# Revit family: Legrand XL³-S 630 24 Modules to the row
name_source: partatom
category: Equipement électrique
units: mm (PartAtom-declared; Revit-internal decimal feet)

## family parameters
Basée sur le plan de construction = Non
Configuration du panneau = Deux colonnes, circuits au sein
Cote de connecteur circulaire = Utiliser le diamètre
Couper avec des vides une fois chargée = Non
Numéro OmniClass = 23.80.30.11.17
Partagée = Non
Point de calcul de pièce = Non
Titre OmniClass = Distribution Boards and Control Panels
Toujours verticalement = Oui
Type d'élément = Tableau de raccordement

## types (11) — shared parameters
ETIM Class 6.0 = EC000261
Fabricant = Legrand
General Conditions of Use = https://export.legrand.com
IK = 08
IP = 40
Image du type = XL3S_630_24M_337582_p_230130.jpg
Material = Steel
RAL = 9003
URL = www.legrand.fr
depth = 249 mm  [stored 0.816929 ft]
depth installation zone = 853 mm  [stored 2.79856 ft]
distance before installation zone = 604 mm  [stored 1.98163 ft]
distance side installation zone = 249 mm  [stored 0.816929 ft]
door = Oui
finish kit = Non
finish kit 337960_337973 = Non
finish kit 337961_337973 = Non
finish kit 337962_337973 = Non
finish kit 337963_337973 = Non
finish kit 337964_337973 = Non
finish kit 337965_337973 = Non
finish kit 337966_337973 = Non
finish kit 337967_337973 = Non
finish kit 337968_337973 = Non
finish kit 337969_337973 = Non
finish kit 337970_337973 = Non
height Base = 100 mm  [stored 0.328084 ft]
left side panel = Oui
plinth = Oui
right side panel = Oui
width = 604 mm  [stored 1.98163 ft]
width installation zone = 1102 mm  [stored 3.61549 ft]
zero-valued in all types: Elévation par défaut

## per-type parameters (varying)
- Distribution envelope - XL³ S 630 Métal - height 750 - 24 modules: Description=Ref 337522 - Distribution envelope - XL³ S 630 Métal - height 750 - 24 modules; door 337642=Oui; door 337652=Non; door 337662=Non; door 337672=Non; door 337682=Non; door 337692=Non; door 337702=Non; door 337712=Non; door 337722=Non; door 337732=Non; door 337742=Non; envelope 337522=Oui; envelope 337532=Non; envelope 337542=Non; envelope 337552=Non; envelope 337562=Non; envelope 337572=Non; envelope 337582=Non; envelope 337592=Non; envelope 337602=Non; envelope 337612=Non; envelope 337622=Non; height=924 mm  [stored 3.0315 ft]; left side panel 337862=Oui; left side panel 337863=Non; left side panel 337864=Non; left side panel 337865=Non; left side panel 337866=Non; left side panel 337867=Non; left side panel 337868=Non; left side panel 337869=Non; left side panel 337870=Non; left side panel 337871=Non; left side panel 337872=Non; right side panel 337862=Oui; right side panel 337863=Non; right side panel 337864=Non; right side panel 337865=Non; right side panel 337866=Non; right side panel 337867=Non; right side panel 337868=Non; right side panel 337869=Non; right side panel 337870=Non; right side panel 337871=Non; right side panel 337872=Non
- Distribution envelope - XL³ S 630 Métal - height 900 - 24 modules: Description=Ref 337532 - Distribution envelope - XL³ S 630 Métal - height 900 - 24 modules; door 337642=Non; door 337652=Oui; door 337662=Non; door 337672=Non; door 337682=Non; door 337692=Non; door 337702=Non; door 337712=Non; door 337722=Non; door 337732=Non; door 337742=Non; envelope 337522=Non; envelope 337532=Oui; envelope 337542=Non; envelope 337552=Non; envelope 337562=Non; envelope 337572=Non; envelope 337582=Non; envelope 337592=Non; envelope 337602=Non; envelope 337612=Non; envelope 337622=Non; height=1074 mm  [stored 3.52362 ft]; left side panel 337862=Non; left side panel 337863=Oui; left side panel 337864=Non; left side panel 337865=Non; left side panel 337866=Non; left side panel 337867=Non; left side panel 337868=Non; left side panel 337869=Non; left side panel 337870=Non; left side panel 337871=Non; left side panel 337872=Non; right side panel 337862=Non; right side panel 337863=Oui; right side panel 337864=Non; right side panel 337865=Non; right side panel 337866=Non; right side panel 337867=Non; right side panel 337868=Non; right side panel 337869=Non; right side panel 337870=Non; right side panel 337871=Non; right side panel 337872=Non
- Distribution envelope - XL³ S 630 Métal - height 1050 - 24 modules: Description=Ref 337542 - Distribution envelope - XL³ S 630 Métal - height 1050 - 24 modules; door 337642=Non; door 337652=Non; door 337662=Oui; door 337672=Non; door 337682=Non; door 337692=Non; door 337702=Non; door 337712=Non; door 337722=Non; door 337732=Non; door 337742=Non; envelope 337522=Non; envelope 337532=Non; envelope 337542=Oui; envelope 337552=Non; envelope 337562=Non; envelope 337572=Non; envelope 337582=Non; envelope 337592=Non; envelope 337602=Non; envelope 337612=Non; envelope 337622=Non; height=1224 mm  [stored 4.01575 ft]; left side panel 337862=Non; left side panel 337863=Non; left side panel 337864=Oui; left side panel 337865=Non; left side panel 337866=Non; left side panel 337867=Non; left side panel 337868=Non; left side panel 337869=Non; left side panel 337870=Non; left side panel 337871=Non; left side panel 337872=Non; right side panel 337862=Non; right side panel 337863=Non; right side panel 337864=Oui; right side panel 337865=Non; right side panel 337866=Non; right side panel 337867=Non; right side panel 337868=Non; right side panel 337869=Non; right side panel 337870=Non; right side panel 337871=Non; right side panel 337872=Non
- Distribution envelope - XL³ S 630 Métal - height 1200 - 24 modules: Description=Ref 337552 - Distribution envelope - XL³ S 630 Métal - height 1200 - 24 modules; door 337642=Non; door 337652=Non; door 337662=Non; door 337672=Oui; door 337682=Non; door 337692=Non; door 337702=Non; door 337712=Non; door 337722=Non; door 337732=Non; door 337742=Non; envelope 337522=Non; envelope 337532=Non; envelope 337542=Non; envelope 337552=Oui; envelope 337562=Non; envelope 337572=Non; envelope 337582=Non; envelope 337592=Non; envelope 337602=Non; envelope 337612=Non; envelope 337622=Non; height=1374 mm  [stored 4.50787 ft]; left side panel 337862=Non; left side panel 337863=Non; left side panel 337864=Non; left side panel 337865=Oui; left side panel 337866=Non; left side panel 337867=Non; left side panel 337868=Non; left side panel 337869=Non; left side panel 337870=Non; left side panel 337871=Non; left side panel 337872=Non; right side panel 337862=Non; right side panel 337863=Non; right side panel 337864=Non; right side panel 337865=Oui; right side panel 337866=Non; right side panel 337867=Non; right side panel 337868=Non; right side panel 337869=Non; right side panel 337870=Non; right side panel 337871=Non; right side panel 337872=Non
- Distribution envelope - XL³ S 630 Métal - height 1350 - 24 modules: Description=Ref 337562 - Distribution envelope - XL³ S 630 Métal - height 1350 - 24 modules; door 337642=Non; door 337652=Non; door 337662=Non; door 337672=Non; door 337682=Oui; door 337692=Non; door 337702=Non; door 337712=Non; door 337722=Non; door 337732=Non; door 337742=Non; envelope 337522=Non; envelope 337532=Non; envelope 337542=Non; envelope 337552=Non; envelope 337562=Oui; envelope 337572=Non; envelope 337582=Non; envelope 337592=Non; envelope 337602=Non; envelope 337612=Non; envelope 337622=Non; height=1524 mm  [stored 5 ft]; left side panel 337862=Non; left side panel 337863=Non; left side panel 337864=Non; left side panel 337865=Non; left side panel 337866=Oui; left side panel 337867=Non; left side panel 337868=Non; left side panel 337869=Non; left side panel 337870=Non; left side panel 337871=Non; left side panel 337872=Non; right side panel 337862=Non; right side panel 337863=Non; right side panel 337864=Non; right side panel 337865=Non; right side panel 337866=Oui; right side panel 337867=Non; right side panel 337868=Non; right side panel 337869=Non; right side panel 337870=Non; right side panel 337871=Non; right side panel 337872=Non
- Distribution envelope - XL³ S 630 Métal - height 1500 - 24 modules: Description=Ref 337572 - Distribution envelope - XL³ S 630 Métal - height 1500 - 24 modules; door 337642=Non; door 337652=Non; door 337662=Non; door 337672=Non; door 337682=Non; door 337692=Oui; door 337702=Non; door 337712=Non; door 337722=Non; door 337732=Non; door 337742=Non; envelope 337522=Non; envelope 337532=Non; envelope 337542=Non; envelope 337552=Non; envelope 337562=Non; envelope 337572=Oui; envelope 337582=Non; envelope 337592=Non; envelope 337602=Non; envelope 337612=Non; envelope 337622=Non; height=1674 mm  [stored 5.49213 ft]; left side panel 337862=Non; left side panel 337863=Non; left side panel 337864=Non; left side panel 337865=Non; left side panel 337866=Non; left side panel 337867=Oui; left side panel 337868=Non; left side panel 337869=Non; left side panel 337870=Non; left side panel 337871=Non; left side panel 337872=Non; right side panel 337862=Non; right side panel 337863=Non; right side panel 337864=Non; right side panel 337865=Non; right side panel 337866=Non; right side panel 337867=Oui; right side panel 337868=Non; right side panel 337869=Non; right side panel 337870=Non; right side panel 337871=Non; right side panel 337872=Non
- Distribution envelope - XL³ S 630 Métal - height 1650 - 24 modules: Description=Ref 337582 - Distribution envelope - XL³ S 630 Métal - height 1650 - 24 modules; door 337642=Non; door 337652=Non; door 337662=Non; door 337672=Non; door 337682=Non; door 337692=Non; door 337702=Oui; door 337712=Non; door 337722=Non; door 337732=Non; door 337742=Non; envelope 337522=Non; envelope 337532=Non; envelope 337542=Non; envelope 337552=Non; envelope 337562=Non; envelope 337572=Non; envelope 337582=Oui; envelope 337592=Non; envelope 337602=Non; envelope 337612=Non; envelope 337622=Non; height=1824 mm  [stored 5.98425 ft]; left side panel 337862=Non; left side panel 337863=Non; left side panel 337864=Non; left side panel 337865=Non; left side panel 337866=Non; left side panel 337867=Non; left side panel 337868=Oui; left side panel 337869=Non; left side panel 337870=Non; left side panel 337871=Non; left side panel 337872=Non; right side panel 337862=Non; right side panel 337863=Non; right side panel 337864=Non; right side panel 337865=Non; right side panel 337866=Non; right side panel 337867=Non; right side panel 337868=Oui; right side panel 337869=Non; right side panel 337870=Non; right side panel 337871=Non; right side panel 337872=Non
- Distribution envelope - XL³ S 630 Métal - height 1800 - 24 modules: Description=Ref 337592 - Distribution envelope - XL³ S 630 Métal - height 1800 - 24 modules; door 337642=Non; door 337652=Non; door 337662=Non; door 337672=Non; door 337682=Non; door 337692=Non; door 337702=Non; door 337712=Oui; door 337722=Non; door 337732=Non; door 337742=Non; envelope 337522=Non; envelope 337532=Non; envelope 337542=Non; envelope 337552=Non; envelope 337562=Non; envelope 337572=Non; envelope 337582=Non; envelope 337592=Oui; envelope 337602=Non; envelope 337612=Non; envelope 337622=Non; height=1974 mm  [stored 6.47638 ft]; left side panel 337862=Non; left side panel 337863=Non; left side panel 337864=Non; left side panel 337865=Non; left side panel 337866=Non; left side panel 337867=Non; left side panel 337868=Non; left side panel 337869=Oui; left side panel 337870=Non; left side panel 337871=Non; left side panel 337872=Non; right side panel 337862=Non; right side panel 337863=Non; right side panel 337864=Non; right side panel 337865=Non; right side panel 337866=Non; right side panel 337867=Non; right side panel 337868=Non; right side panel 337869=Oui; right side panel 337870=Non; right side panel 337871=Non; right side panel 337872=Non
- Distribution envelope - XL³ S 630 Métal - height 1950 - 24 modules: Description=Ref 337602 - Distribution envelope - XL³ S 630 Métal - height 1950 - 24 modules; door 337642=Non; door 337652=Non; door 337662=Non; door 337672=Non; door 337682=Non; door 337692=Non; door 337702=Non; door 337712=Non; door 337722=Oui; door 337732=Non; door 337742=Non; envelope 337522=Non; envelope 337532=Non; envelope 337542=Non; envelope 337552=Non; envelope 337562=Non; envelope 337572=Non; envelope 337582=Non; envelope 337592=Non; envelope 337602=Oui; envelope 337612=Non; envelope 337622=Non; height=2124 mm  [stored 6.9685 ft]; left side panel 337862=Non; left side panel 337863=Non; left side panel 337864=Non; left side panel 337865=Non; left side panel 337866=Non; left side panel 337867=Non; left side panel 337868=Non; left side panel 337869=Non; left side panel 337870=Oui; left side panel 337871=Non; left side panel 337872=Non; right side panel 337862=Non; right side panel 337863=Non; right side panel 337864=Non; right side panel 337865=Non; right side panel 337866=Non; right side panel 337867=Non; right side panel 337868=Non; right side panel 337869=Non; right side panel 337870=Oui; right side panel 337871=Non; right side panel 337872=Non
- Distribution envelope - XL³ S 630 Métal - height 2100 - 24 modules: Description=Ref 337612 - Distribution envelope - XL³ S 630 Métal - height 2100 - 24 modules; door 337642=Non; door 337652=Non; door 337662=Non; door 337672=Non; door 337682=Non; door 337692=Non; door 337702=Non; door 337712=Non; door 337722=Non; door 337732=Oui; door 337742=Non; envelope 337522=Non; envelope 337532=Non; envelope 337542=Non; envelope 337552=Non; envelope 337562=Non; envelope 337572=Non; envelope 337582=Non; envelope 337592=Non; envelope 337602=Non; envelope 337612=Oui; envelope 337622=Non; height=2274 mm  [stored 7.46063 ft]; left side panel 337862=Non; left side panel 337863=Non; left side panel 337864=Non; left side panel 337865=Non; left side panel 337866=Non; left side panel 337867=Non; left side panel 337868=Non; left side panel 337869=Non; left side panel 337870=Non; left side panel 337871=Oui; left side panel 337872=Non; right side panel 337862=Non; right side panel 337863=Non; right side panel 337864=Non; right side panel 337865=Non; right side panel 337866=Non; right side panel 337867=Non; right side panel 337868=Non; right side panel 337869=Non; right side panel 337870=Non; right side panel 337871=Oui; right side panel 337872=Non
- Distribution envelope - XL³ S 630 Métal - height 2250 - 24 modules: Description=Ref 337622 - Distribution envelope - XL³ S 630 Métal - height 2250 - 24 modules; door 337642=Non; door 337652=Non; door 337662=Non; door 337672=Non; door 337682=Non; door 337692=Non; door 337702=Non; door 337712=Non; door 337722=Non; door 337732=Non; door 337742=Oui; envelope 337522=Non; envelope 337532=Non; envelope 337542=Non; envelope 337552=Non; envelope 337562=Non; envelope 337572=Non; envelope 337582=Non; envelope 337592=Non; envelope 337602=Non; envelope 337612=Non; envelope 337622=Oui; height=2424 mm  [stored 7.95276 ft]; left side panel 337862=Non; left side panel 337863=Non; left side panel 337864=Non; left side panel 337865=Non; left side panel 337866=Non; left side panel 337867=Non; left side panel 337868=Non; left side panel 337869=Non; left side panel 337870=Non; left side panel 337871=Non; left side panel 337872=Oui; right side panel 337862=Non; right side panel 337863=Non; right side panel 337864=Non; right side panel 337865=Non; right side panel 337866=Non; right side panel 337867=Non; right side panel 337868=Non; right side panel 337869=Non; right side panel 337870=Non; right side panel 337871=Non; right side panel 337872=Oui

note: [stored X ft] marks values corroborated as IEEE doubles in the binary element streams (Revit-internal decimal feet)
